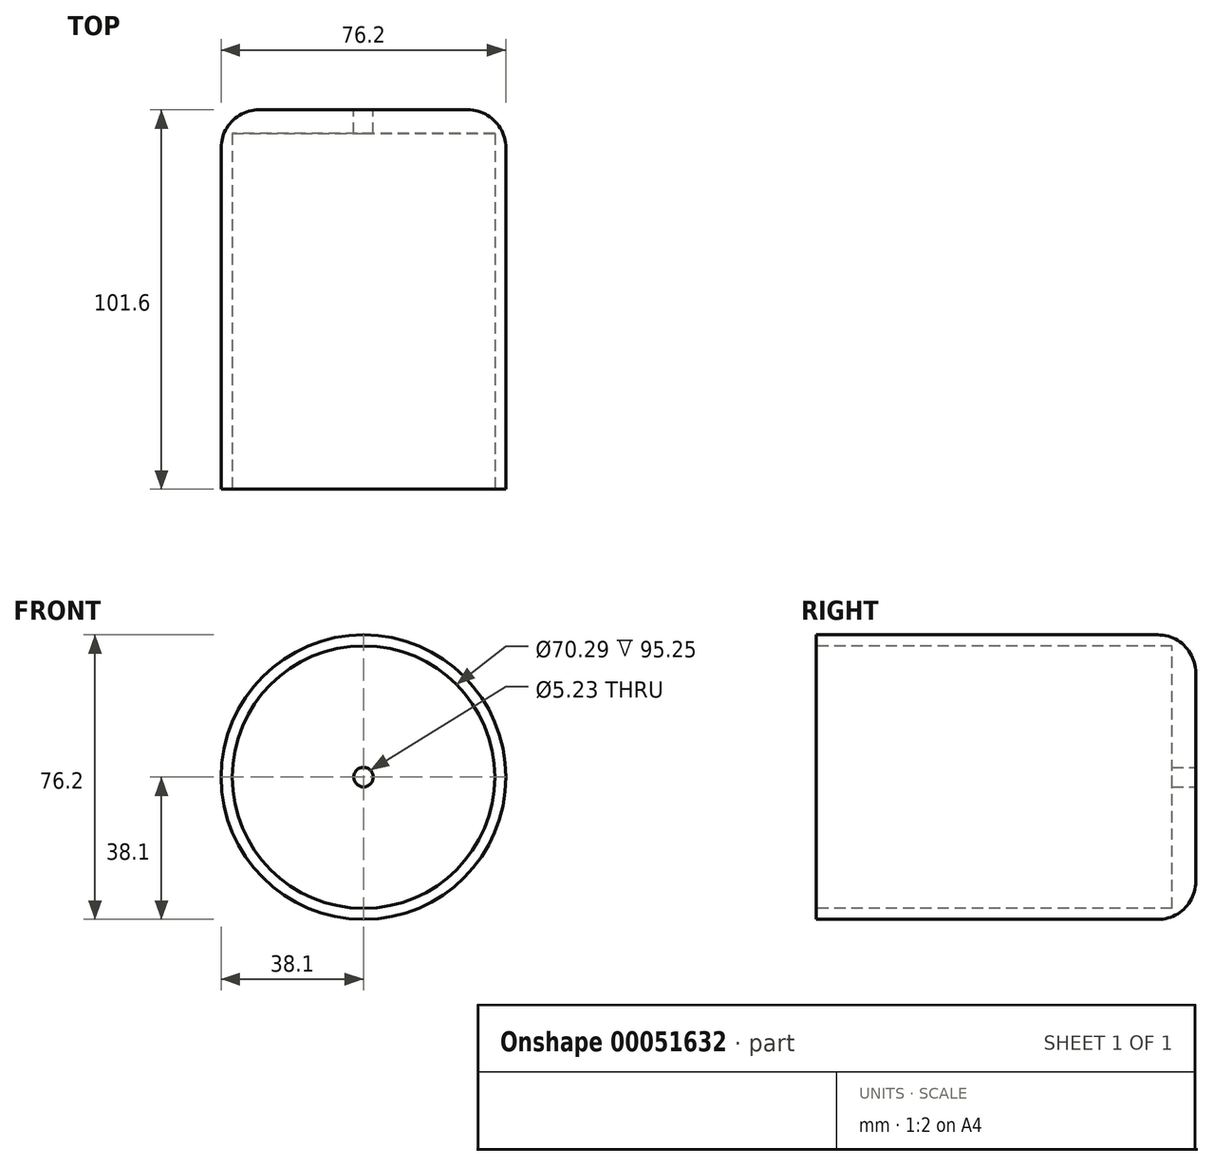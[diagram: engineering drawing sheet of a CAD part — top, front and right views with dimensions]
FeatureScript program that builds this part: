
annotation { "Feature Type Name" : "Feature", "Feature Type Description" : "" }
export const myFeature = defineFeature(function(context is Context, id is Id, definition is map)
    precondition{}
    {
        {
            var Q0;
            Q0=qCreatedBy(makeId("Front.planeOp"),FACE);
            var sketch = newSketch(context, id + "F0", { "sketchPlane" : qUnion([Q0])});
            skCircle(sketch, "E0", {"center": v(0, 0) * mm, "radius": 38.1 * mm});
            skCircle(sketch, "E1", {"center": v(0, 0) * mm, "radius": 34.06 * mm});
            skSolve(sketch);
        }
        {
            var Q0;
            Q0=makeQuery(id+"F0.imprint","IMPRINT",FACE,{"disambiguationData":[TD([[makeQuery(id+"F0.imprint","IMPRINT",EDGE,{"derivedFrom":sQuery(id+"F0.wireOp",EDGE,"E1")}),1.0]])]});
            var Q1;
            Q1=makeQuery(id+"F0.imprint","IMPRINT",FACE,{"disambiguationData":[TD([[makeQuery(id+"F0.imprint","IMPRINT",EDGE,{"derivedFrom":sQuery(id+"F0.wireOp",EDGE,"E0")}),1.0]])]});
            extrude(context, id + "F1", {"entities" : qUnion([Q0, Q1]), "depth" : 101.6 * mm});
        }
        {
            var Q0;
            Q0=makeQuery(id+"F1.opExtrude","CAP_FACE",FACE,{"disambiguationData":[OSD([sQuery(id+"F0.wireOp",EDGE,"E0")])],"isStart":false});
            var sketch = newSketch(context, id + "F2", { "sketchPlane" : qUnion([Q0])});
            skCircle(sketch, "E2", {"center": v(0, 0) * mm, "radius": 35.15 * mm});
            skSolve(sketch);
        }
        {
            var Q0;
            Q0=makeQuery(id+"F2.imprint","IMPRINT",FACE,{"disambiguationData":[TD([[makeQuery(id+"F2.imprint","IMPRINT",EDGE,{"derivedFrom":sQuery(id+"F2.wireOp",EDGE,"E2")}),1.0]])]});
            extrude(context, id + "F3", {"entities" : qUnion([Q0]), "operationType" : NewBodyOperationType.REMOVE, "oppositeDirection" : true, "depth" : 95.25 * mm});
        }
        {
            var Q0;
            Q0=makeQuery(id+"F1.opExtrude","CAP_EDGE",EDGE,{"disambiguationData":[OSD([sQuery(id+"F0.wireOp",EDGE,"E0")])],"isStart":true});
            fillet(context, id + "F4", {"entities" : qUnion([Q0]), "radius" : 10.16 * mm, "tangentPropagation" : true, "allowEdgeOverflow" : false});
        }
        {
            var Q0;
            Q0=qCreatedBy(makeId("Front.planeOp"),FACE);
            var sketch = newSketch(context, id + "F5", { "sketchPlane" : qUnion([Q0])});
            skCircle(sketch, "E3", {"center": v(0, 0) * mm, "radius": 2.61 * mm});
            skSolve(sketch);
        }
        {
            var Q0;
            Q0 = qSketchRegion(id + "F5", true);
            extrude(context, id + "F6", {"entities" : qUnion([Q0]), "operationType" : NewBodyOperationType.REMOVE, "endBound" : BoundingType.THROUGH_ALL, "depth" : 25.4 * mm});
        }
    });
